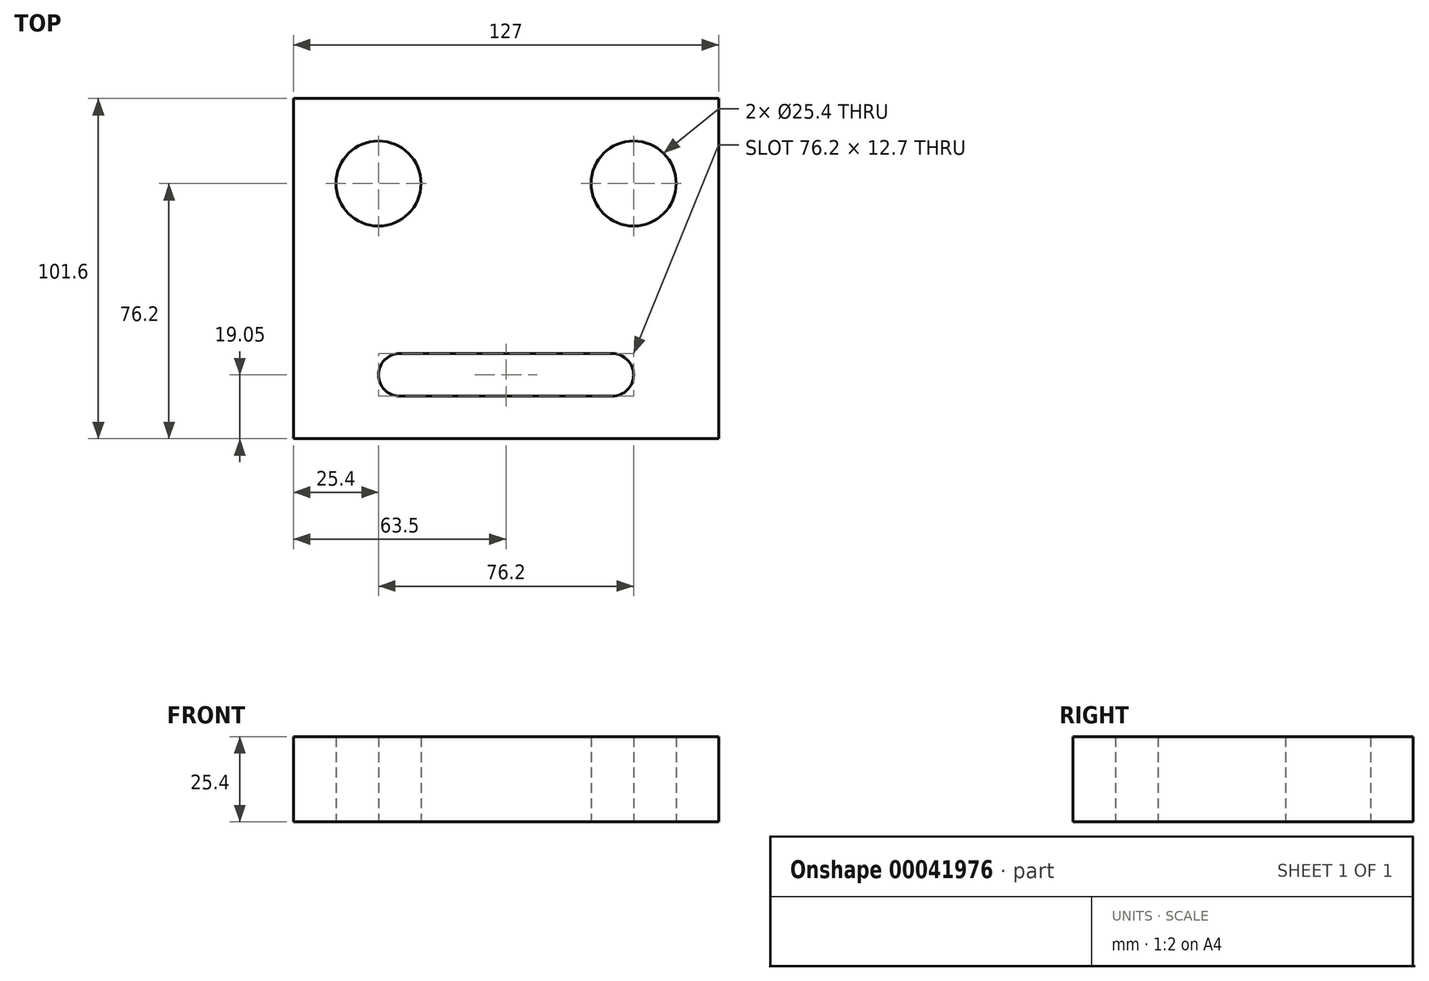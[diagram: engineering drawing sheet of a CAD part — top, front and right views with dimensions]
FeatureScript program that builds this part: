
annotation { "Feature Type Name" : "Feature", "Feature Type Description" : "" }
export const myFeature = defineFeature(function(context is Context, id is Id, definition is map)
    precondition{}
    {
        {
            var Q0;
            Q0=qCreatedBy(makeId("Top.planeOp"),FACE);
            var sketch = newSketch(context, id + "F0", { "sketchPlane" : qUnion([Q0])});
            skLineSegment(sketch, "E0.bottom", {"start": v(0, 0) * mm, "end": v(127, 0) * mm});
            skLineSegment(sketch, "E0.top", {"start": v(0, -101.6) * mm, "end": v(127, -101.6) * mm});
            skLineSegment(sketch, "E0.left", {"start": v(0, 0) * mm, "end": v(0, -101.6) * mm});
            skLineSegment(sketch, "E0.right", {"start": v(127, 0) * mm, "end": v(127, -101.6) * mm});
            skLineSegment(sketch, "E1.bottom", {"start": v(31.75, -76.2) * mm, "end": v(95.25, -76.2) * mm});
            skLineSegment(sketch, "E1.top", {"start": v(31.75, -88.9) * mm, "end": v(95.25, -88.9) * mm});
            skLineSegment(sketch, "E1.left", {"start": v(25.4, -82.55) * mm, "end": v(25.4, -82.55) * mm});
            skLineSegment(sketch, "E1.right", {"start": v(101.6, -82.55) * mm, "end": v(101.6, -82.55) * mm});
            skPoint(sketch, "E2.visualSharp", {"position": v(25.4, -76.2) * mm});
            skArc(sketch, "E2.filletArc", {"start": v(31.75, -76.2) * mm, "mid": v(27.26, -78.06) * mm, "end": v(25.4, -82.55) * mm});
            skPoint(sketch, "E3.visualSharp", {"position": v(25.4, -88.9) * mm});
            skArc(sketch, "E3.filletArc", {"start": v(25.4, -82.55) * mm, "mid": v(27.26, -87.04) * mm, "end": v(31.75, -88.9) * mm});
            skPoint(sketch, "E4.visualSharp", {"position": v(101.6, -88.9) * mm});
            skArc(sketch, "E4.filletArc", {"start": v(95.25, -88.9) * mm, "mid": v(99.74, -87.04) * mm, "end": v(101.6, -82.55) * mm});
            skPoint(sketch, "E5.visualSharp", {"position": v(101.6, -76.2) * mm});
            skArc(sketch, "E5.filletArc", {"start": v(101.6, -82.55) * mm, "mid": v(99.74, -78.06) * mm, "end": v(95.25, -76.2) * mm});
            skCircle(sketch, "E6", {"center": v(25.4, -25.4) * mm, "radius": 12.7 * mm});
            skCircle(sketch, "E7", {"center": v(101.6, -25.4) * mm, "radius": 12.7 * mm});
            skSolve(sketch);
        }
        {
            var Q0;
            Q0=makeQuery(id+"F0.imprint","IMPRINT",FACE,{"disambiguationData":[TD([[makeQuery(id+"F0.imprint","IMPRINT",EDGE,{"derivedFrom":sQuery(id+"F0.wireOp",EDGE,"E0.bottom")}),-1.0]])]});
            extrude(context, id + "F1", {"entities" : qUnion([Q0]), "depth" : 25.4 * mm});
        }
    });
